# Revit family: Haworth_JiveTable_HalfHexagon
name_source: partatom
category: Furniture Systems
revit_build: Autodesk Revit 2018 (Build: 20170223_1515(x64)
units: mm (PartAtom-declared; Revit-internal decimal feet)

## family parameters
Always vertical = Yes
Cut with Voids When Loaded = No
OmniClass Number = 23.40.70.14.64.21
OmniClass Title = Systems Furniture
Part Type = Normal
Room Calculation Point = No
Round Connector Dimension = Use Diameter
Shared = No
Work Plane-Based = No

## types (4) — shared parameters
Actual Depth = 48"
Actual Width = 48"
Actual Width 2 = 24"
Assembly Code = E2020200
Custom Size = No
Leg Finish = Haworth _ Paint _ Graphite
Manufacturer = Haworth, Inc.
Max. Height = 42"
Min. Height = 29"
Model = Haworth Jive
Revision Number = 0
Size = Verify Final Dim. w/ Haworth
Standard Depths = 48 in.
Standard Height = 29, 42 in.
Standard Widths = 48 in.
Table Edge Finish = Haworth _ Laminate _ Putty H-AA
Table Finish = Haworth _ Laminate _ Putty H-AA
Table Thickness = 1 3/16"
URL = http://www.haworth.com
URL - Product = http://www.haworth.com
Warranty = http://www.haworth.com

## per-type parameters (varying)
| type | Actual Height | Casters | Description | Glides | Height | Leg Height |
| 48d 48w 29h - With Casters | 29" | Yes | Haworth Jive Table Half Hexagon - 48d 48w 29h - With Casters | No | 29" | 27 13/16" |
| 48d 48w 29h - With Glides | 29" | No | Haworth Jive Table Half Hexagon - 48d 48w 29h - With Glides | Yes | 29" | 27 13/16" |
| 48d 48w 42h - With Glides | 42" | No | Haworth Jive Table Half Hexagon - 48d 48w 42h - With Glides | Yes | 42" | 40 13/16" |
| 48d 48w 42h - With Casters | 42" | Yes | Haworth Jive Table Half Hexagon - 48d 48w 42h - With Casters | No | 42" | 40 13/16" |

## geometry (parser evidence)
native form markers: Sweep x17
no freeform markers — native parametric forms only
